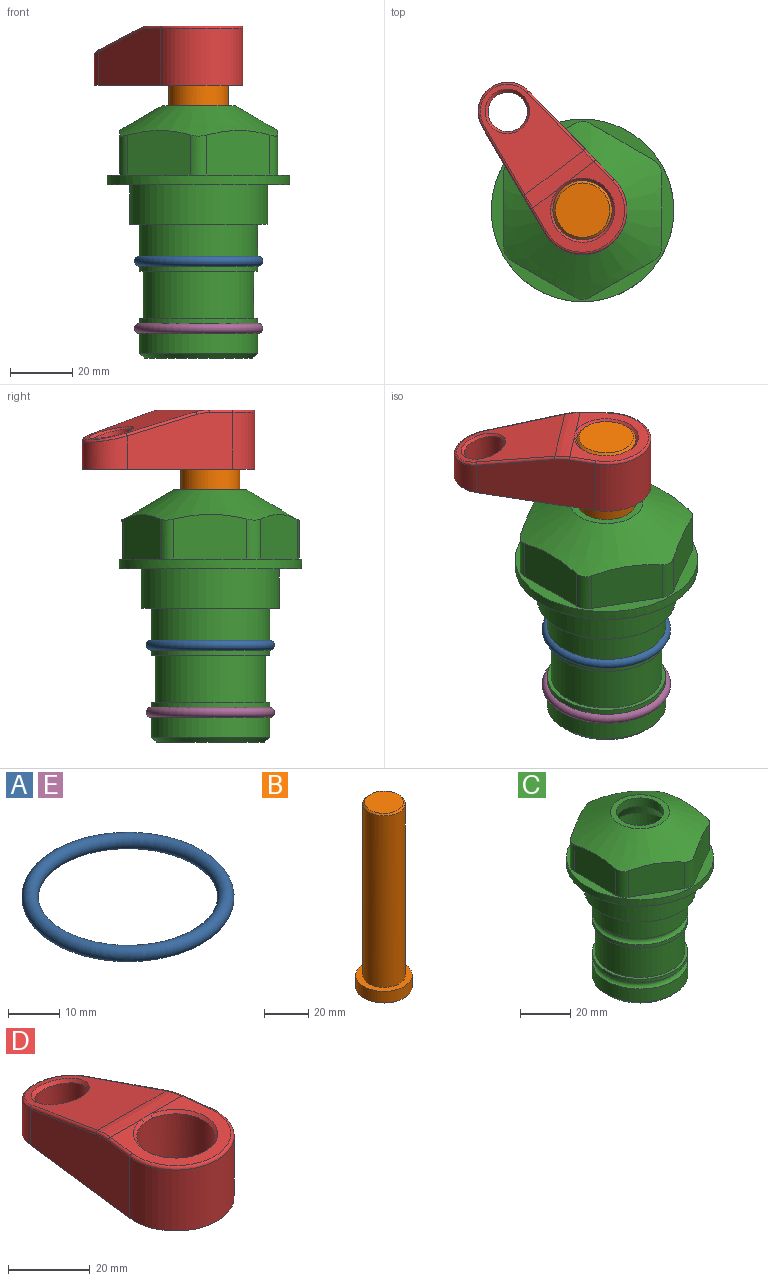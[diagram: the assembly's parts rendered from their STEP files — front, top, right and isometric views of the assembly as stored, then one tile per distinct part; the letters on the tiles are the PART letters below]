
ASSEMBLY  parts=5 mates=3
PART A: 1 faces, bbox 44.7x44.7x3.2 mm
  f0: torus R=19.05mm, axis (0,0,1), area 1193.9mm2
PART B: 6 faces, bbox 25.4x25.4x101.6 mm
  f0: plane 17.46x17.46mm, normal (0,0,1), area 239.5mm2, adj f5
  f1: plane 25.4x25.4mm, normal (0,0,-1), area 506.7mm2, adj f2
  f2: cylinder r=12.7mm len=25.4mm, axis (0,0,1), area 506.7mm2, adj f1,f3
  f3: plane 25.4x25.4mm, normal (0,0,1), area 221.7mm2, adj f2,f4
  f4: cylinder r=9.53mm len=94.46mm, axis (0,0,1), area 5653mm2, adj f3,f5
  f5: cone r=8.73mm half-angle=45deg, axis (0,0,-1), area 64.4mm2, adj f0,f4
PART C: 36 faces, bbox 58.7x58.7x81 mm
  f0: cylinder r=17.78mm len=35.56mm, axis (0,0,1), area 1670.8mm2, adj f23,f24,f31
  f1: cylinder r=19.05mm len=38.1mm, axis (0,0,1), area 1191.9mm2, adj f26,f27,f30
  f2: plane 58.66x58.66mm, normal (0,0,-1), area 1150.6mm2, adj f3,f28
  f3: cylinder r=29.33mm len=58.66mm, axis (0,0,-1), area 585.1mm2, adj f2,f4
  f4: plane 58.66x58.66mm, normal (0,0,1), area 475.9mm2, adj f3,f5,f6,f7,f8,f9,f10,f11
  f5: plane 20.32x14.34mm, normal (-0.5,0.87,0), area 324.4mm2, adj f4,f15,f16,f17
  f6: plane 20.32x14.34mm, normal (0.5,0.87,0), area 324.4mm2, adj f4,f14,f15,f17
  f7: plane 23.48x14.34mm, normal (1,0,0), area 324.4mm2, adj f4,f13,f14,f17
  f8: plane 20.32x14.34mm, normal (0.5,-0.87,0), area 324.4mm2, adj f4,f12,f13,f17
  f9: plane 20.32x14.34mm, normal (-0.5,-0.87,0), area 324.4mm2, adj f4,f11,f12,f17
  f10: plane 23.48x14.34mm, normal (-1,0,0), area 324.4mm2, adj f4,f11,f16,f17
  f11: cylinder r=5.08mm len=12.85mm, axis (0,0,-1), area 67.2mm2, adj f4,f9,f10,f17
  f12: cylinder r=5.08mm len=12.85mm, axis (0,0,-1), area 67.2mm2, adj f4,f8,f9,f17
  f13: cylinder r=5.08mm len=12.85mm, axis (0,0,-1), area 67.2mm2, adj f4,f7,f8,f17
  f14: cylinder r=5.08mm len=12.85mm, axis (0,0,-1), area 67.2mm2, adj f4,f6,f7,f17
  f15: cylinder r=5.08mm len=12.85mm, axis (0,0,-1), area 67.2mm2, adj f4,f5,f6,f17
  f16: cylinder r=5.08mm len=12.85mm, axis (0,0,-1), area 67.2mm2, adj f4,f5,f10,f17
  f17: cone r=11.73mm half-angle=60deg, axis (0,0,-1), area 2071.8mm2, adj f5,f6,f7,f8,f9,f10,f11,f12
  f18: plane 23.46x23.46mm, normal (0,0,1), area 147.4mm2, adj f17,f35
  f19: plane 34.93x34.93mm, normal (0,0,-1), area 958mm2, adj f29
  f20: cylinder r=19.05mm len=38.1mm, axis (0,0,1), area 760.1mm2, adj f21,f29
  f21: torus R=19.05mm, axis (0,0,1), area 565.3mm2, adj f20,f22
  f22: cylinder r=19.05mm len=38.1mm, axis (0,0,1), area 190mm2, adj f21,f23
  f23: plane 38.1x38.1mm, normal (0,0,1), area 146.9mm2, adj f0,f22
  f24: plane 38.1x38.1mm, normal (0,0,-1), area 146.9mm2, adj f0,f25
  f25: cylinder r=19.05mm len=38.1mm, axis (0,0,1), area 190mm2, adj f24,f26
  f26: torus R=19.05mm, axis (0,0,1), area 565.3mm2, adj f1,f25
  f27: plane 44.45x44.45mm, normal (0,0,-1), area 411.7mm2, adj f1,f28
  f28: cylinder r=22.23mm len=44.45mm, axis (0,0,1), area 1773.5mm2, adj f2,f27
  f29: cone r=19.05mm half-angle=45deg, axis (0,0,1), area 257.5mm2, adj f19,f20
  f30: cylinder r=3.17mm len=6.75mm, axis (-1,0,0), area 128mm2, adj f1,f33
  f31: cylinder r=3.17mm len=6.35mm, axis (-1,0,0), area 102.5mm2, adj f0,f33
  f32: plane 25.4x25.4mm, normal (0,0,1), area 506.7mm2, adj f33
  f33: cylinder r=12.7mm len=66.42mm, axis (0,0,-1), area 5236.2mm2, adj f30,f31,f32,f34
  f34: cone r=9.53mm half-angle=30deg, axis (0,0,-1), area 443.4mm2, adj f33,f35
  f35: cylinder r=9.53mm len=19.05mm, axis (0,0,-1), area 240.9mm2, adj f18,f34
PART D: 31 faces, bbox 31.7x65.5x19.8 mm
  f0: plane 39.12x18.26mm, normal (0.99,0.12,0), area 612.2mm2, adj f1,f4,f7,f11,f13,f15
  f1: cylinder r=9.53mm len=18.91mm, axis (0,0,-1), area 296.1mm2, adj f0,f2,f7,f17
  f2: plane 39.12x18.26mm, normal (-0.99,0.12,0), area 612.2mm2, adj f1,f4,f7,f12,f14,f16
  f3: cylinder r=6.35mm len=12.7mm, axis (0,0,-1), area 362.4mm2, adj f7,f18
  f4: cylinder r=14.29mm len=28.58mm, axis (0,0,-1), area 882.2mm2, adj f0,f2,f7,f10
  f5: cylinder r=9.53mm len=19.05mm, axis (0,0,-1), area 1092.6mm2, adj f7,f19,f20
  f6: plane 26.99x23.69mm, normal (0,0,1), area 216.2mm2, adj f9,f10,f11,f12,f19
  f7: plane 63.5x28.58mm, normal (0,0,-1), area 661.8mm2, adj f0,f1,f2,f3,f4,f5,f22,f23
  f8: plane 33.52x23.6mm, normal (0,0.26,0.97), area 486mm2, adj f9,f15,f16,f17,f18
  f9: cylinder r=19.05mm len=24.72mm, axis (1,0,0), area 120.4mm2, adj f6,f8,f13,f14,f20
  f10: torus R=13.49mm, axis (0,0,1), area 59mm2, adj f4,f6,f11,f12
  f11: cylinder r=0.79mm len=8.67mm, axis (0.12,-0.99,0), area 10.8mm2, adj f0,f6,f10,f13
  f12: cylinder r=0.79mm len=8.67mm, axis (0.12,0.99,0), area 10.8mm2, adj f2,f6,f10,f14
  f13: bspline ~4.95x1.42mm, area 6.1mm2, adj f0,f9,f11,f15
  f14: bspline ~4.95x1.42mm, area 6.1mm2, adj f2,f9,f12,f16
  f15: cylinder r=0.79mm len=25.95mm, axis (0.12,-0.96,0.26), area 32.9mm2, adj f0,f8,f13,f17
  f16: cylinder r=0.79mm len=25.95mm, axis (0.12,0.96,-0.26), area 32.9mm2, adj f2,f8,f14,f17
  f17: bspline ~18.91x8.38mm, area 30mm2, adj f1,f8,f15,f16
  f18: bspline ~14.29x14.29mm, area 48.3mm2, adj f3,f8
  f19: cone r=9.53mm half-angle=45deg, axis (0,0,1), area 66.5mm2, adj f5,f6,f20
  f20: bspline ~3.22x0.96mm, area 3.5mm2, adj f5,f9,f19
  f21: plane 2.75x2.72mm, normal (0,0,-1), area 2.9mm2, adj f23,f25,f28
  f22: plane 23.05x15.88mm, normal (-0.99,-0.12,0), area 323.6mm2, adj f7,f25,f26,f27,f28,f29
  f23: plane 23.05x15.88mm, normal (0.99,-0.12,0), area 323.6mm2, adj f7,f21,f25,f27,f28,f30
  f24: cylinder r=9.53mm len=10.69mm, axis (0,0,-1), area 114.7mm2, adj f7,f27,f29,f30
  f25: cylinder r=12.7mm len=20.59mm, axis (0,0,-1), area 381.1mm2, adj f7,f21,f22,f23,f26,f28
  f26: plane 2.75x2.72mm, normal (0,0,-1), area 2.9mm2, adj f22,f25,f28
  f27: plane 19.72x18.37mm, normal (0,-0.26,-0.97), area 291.8mm2, adj f22,f23,f24,f28,f29,f30
  f28: cylinder r=15.88mm len=19.92mm, axis (1,0,0), area 54.8mm2, adj f21,f22,f23,f25,f26,f27
  f29: cylinder r=1.59mm len=11mm, axis (0,0,-1), area 34.7mm2, adj f7,f22,f24,f27
  f30: cylinder r=1.59mm len=11mm, axis (0,0,-1), area 34.7mm2, adj f7,f23,f24,f27
PART E: same geometry as A
PLACE A t=(0,0,55.63)mm
PLACE B rot(axis=(0,0,1),37.3deg) t=(0,0,43.18)mm
PLACE C t=(0,0,55.63)mm fixed
PLACE D rot(axis=(0,0,1),37.3deg) t=(0,0,43.18)mm
PLACE E t=(0,0,34.04)mm
MATE fastened A.f0 <-> C.f0  axis (0,0,1) through (0,0,31.12)mm
MATE cylindrical B.f2 <-> C.f0  axis (0,0,-1) through (0,0,5.08)mm
MATE fastened E.f0 <-> C.f0  axis (0,0,1) through (0,0,9.53)mm
